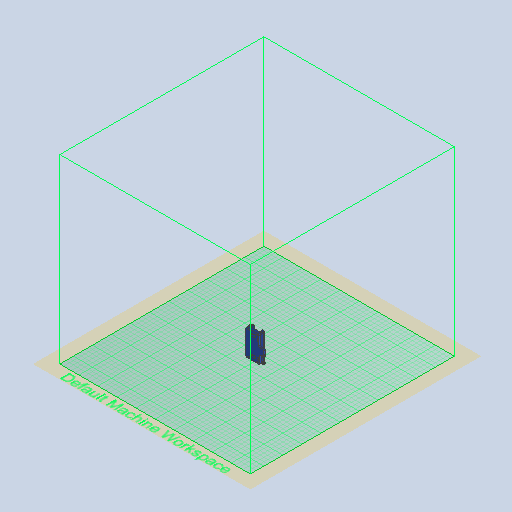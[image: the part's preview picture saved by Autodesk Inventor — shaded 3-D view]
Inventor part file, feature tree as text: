
AUTODESK INVENTOR PART (.ipt)
format: ipt  version: 2022 (Build 260153000, 153)  size: 977,920 bytes
history: native  units: mm
features: extrude x7, other x6, sketch x6, fillet x4, projected_geometry x1
ambient origin geometry x8: Origin, YZ Plane, XZ Plane, XY Plane, X Axis, Y Axis, Z Axis, Center Point
bodies: Body1 (feature_tree)
feature tree (24):
  other  "Твердое тело1"
  other  "РабПлоскость1"
  extrude  "Выдавливание1"  Depth=37.7mm
  fillet  "Сопряжение1"  Radius=57.4mm
  extrude  "Выдавливание2"  Depth=10.0mm
  sketch  "Эскиз3"
  extrude  "Выдавливание3"  Depth=6.0mm
  fillet  "Сопряжение3"  Radius=6.0mm
  fillet  "Сопряжение4"  Radius=2.0mm
  extrude  "Выдавливание4"  Depth=16.8mm
  extrude  "Выдавливание5"  Depth=12.0mm
  other  "РабПлоскость2"
  extrude  "Выдавливание6"  Depth=15.0mm
  extrude  "Выдавливание7"  Depth=20.2mm
  fillet  "Сопряжение6"  Radius=28.5mm
  sketch  "Эскиз1"
  sketch  "Эскиз2"
  projected_geometry  "Спроецированная петля1"
  sketch  "Эскиз4"
  sketch  "Эскиз5"
  sketch  "Эскиз6"
  other  "<userpath>\Documents\Inventor\Aim.iam"
  other  "Aim.iam"
  other  "Bottom:1"
